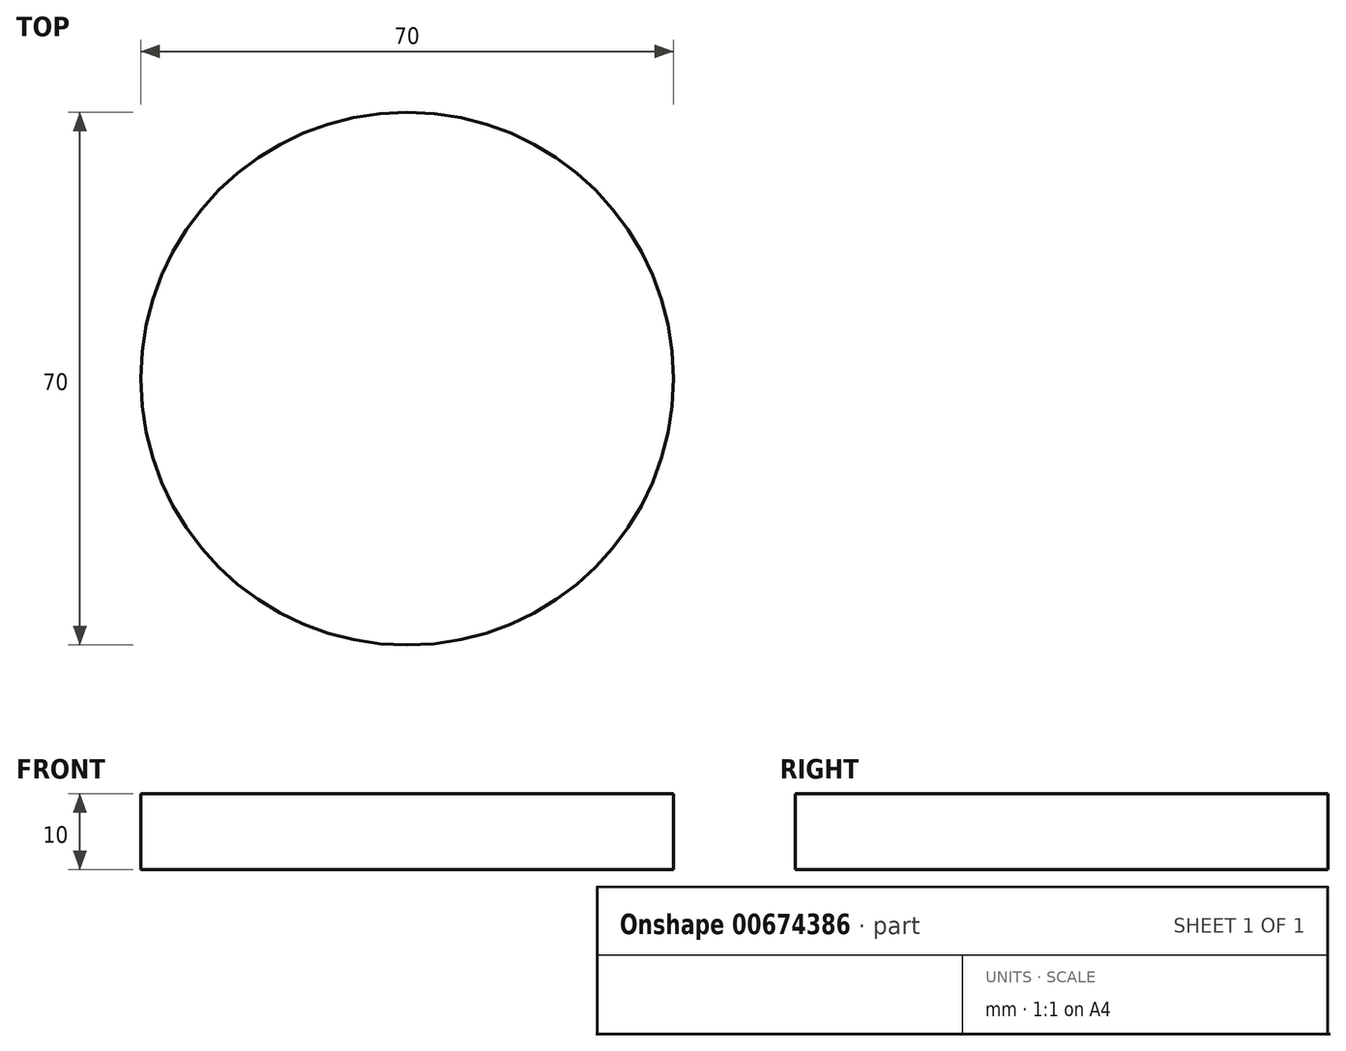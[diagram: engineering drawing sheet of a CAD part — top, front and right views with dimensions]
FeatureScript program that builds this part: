
annotation { "Feature Type Name" : "Feature", "Feature Type Description" : "" }
export const myFeature = defineFeature(function(context is Context, id is Id, definition is map)
    precondition{}
    {
        {
            var Q0;
            Q0=qCreatedBy(makeId("Top.planeOp"),FACE);
            var sketch = newSketch(context, id + "F0", { "sketchPlane" : qUnion([Q0])});
            skCircle(sketch, "E0", {"center": v(0, 0) * mm, "radius": 35 * mm});
            skSolve(sketch);
        }
        {
            var Q0;
            Q0=makeQuery(id+"F0.imprint","IMPRINT",FACE,{"disambiguationData":[TD([[makeQuery(id+"F0.imprint","IMPRINT",EDGE,{"derivedFrom":sQuery(id+"F0.wireOp",EDGE,"E0")}),1.0]])]});
            extrude(context, id + "F1", {"entities" : qUnion([Q0]), "depth" : 10 * mm, "offsetDistance" : 25.4 * mm});
        }
    });
